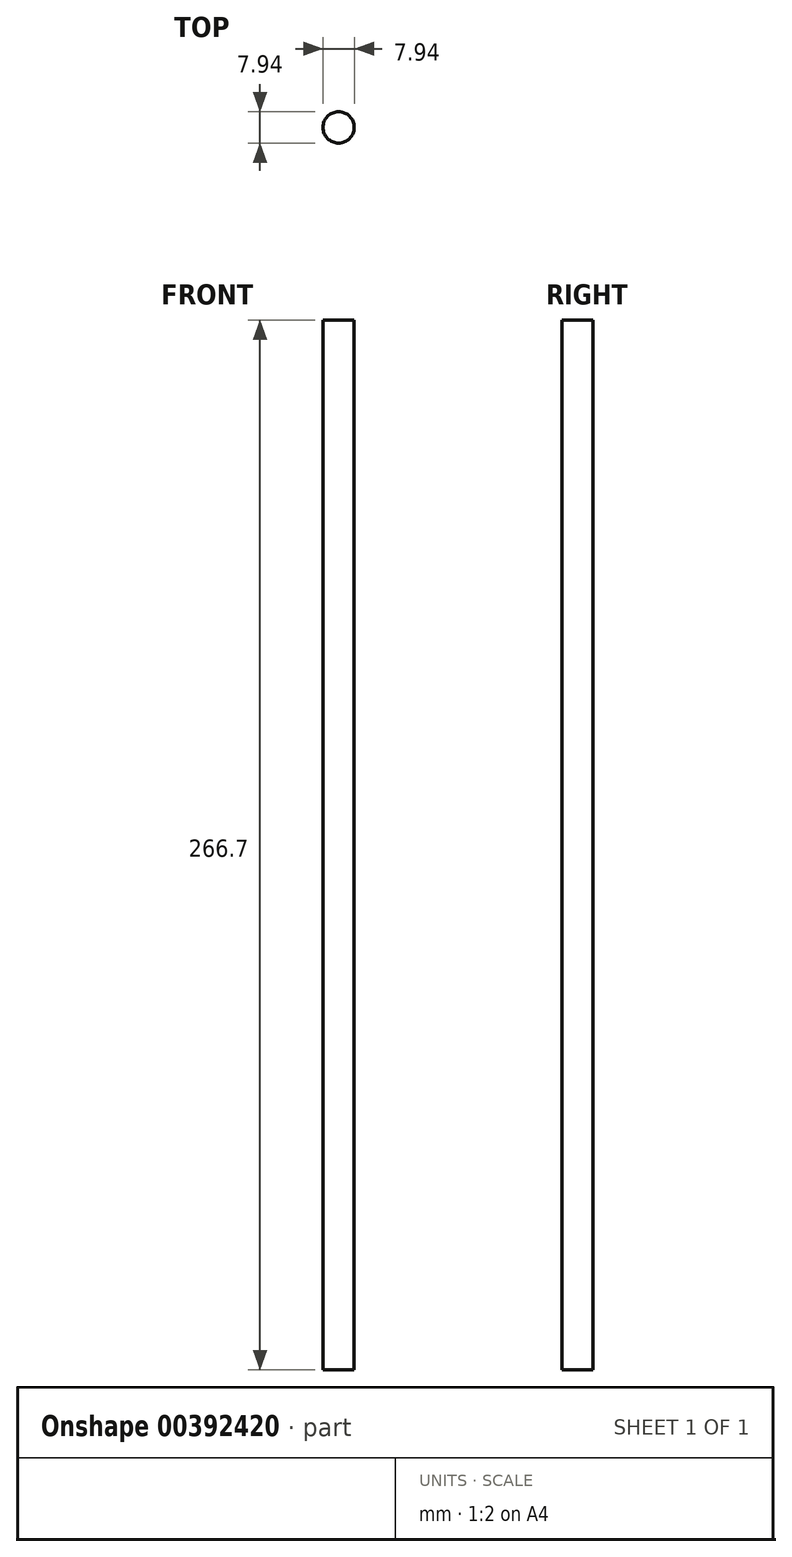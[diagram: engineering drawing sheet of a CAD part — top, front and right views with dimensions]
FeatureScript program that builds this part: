
annotation { "Feature Type Name" : "Feature", "Feature Type Description" : "" }
export const myFeature = defineFeature(function(context is Context, id is Id, definition is map)
    precondition{}
    {
        {
            var Q0;
            Q0=qCreatedBy(makeId("Top.planeOp"),FACE);
            var sketch = newSketch(context, id + "F0", { "sketchPlane" : qUnion([Q0])});
            skCircle(sketch, "E0", {"center": v(-34.47, -43.18) * mm, "radius": 3.97 * mm});
            skSolve(sketch);
        }
        {
            var Q0;
            Q0 = qSketchRegion(id + "F0", true);
            extrude(context, id + "F1", {"entities" : qUnion([Q0]), "depth" : 266.7 * mm});
        }
    });
